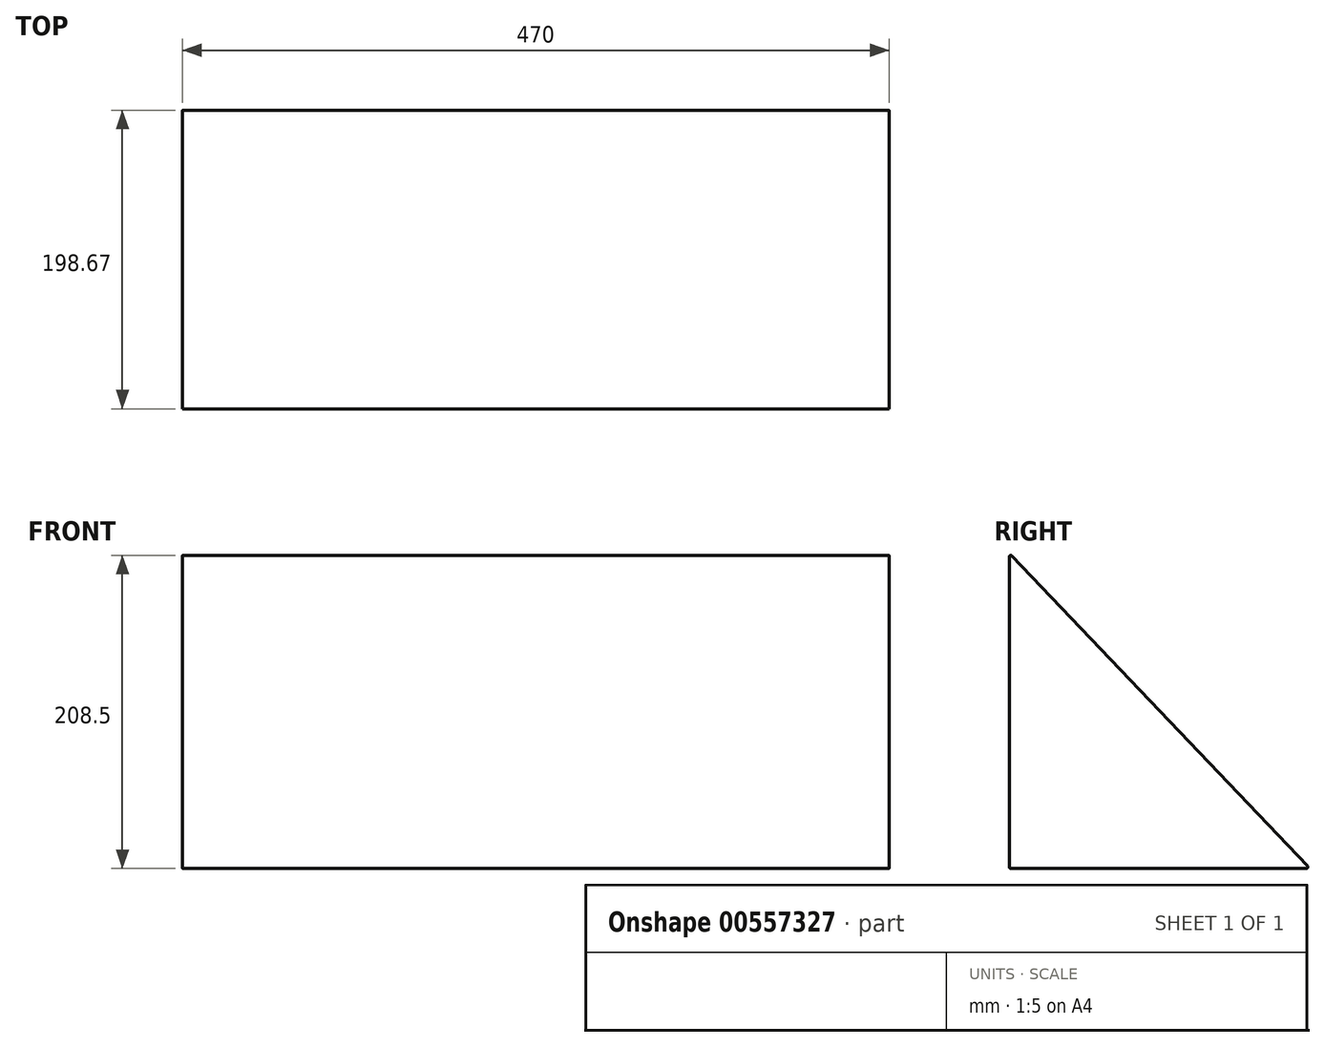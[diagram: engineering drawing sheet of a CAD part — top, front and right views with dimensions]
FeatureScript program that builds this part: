
annotation { "Feature Type Name" : "Feature", "Feature Type Description" : "" }
export const myFeature = defineFeature(function(context is Context, id is Id, definition is map)
    precondition{}
    {
        {
            var Q0;
            Q0=qCreatedBy(makeId("Right.planeOp"),FACE);
            var sketch = newSketch(context, id + "F0", { "sketchPlane" : qUnion([Q0])});
            skLineSegment(sketch, "E0", {"start": v(0, 0) * mm, "end": v(0, 210) * mm});
            skLineSegment(sketch, "E1", {"start": v(0, 210) * mm, "end": v(200, 0) * mm});
            skLineSegment(sketch, "E2", {"start": v(200, 0) * mm, "end": v(0, 0) * mm});
            skSolve(sketch);
        }
        {
            var Q0;
            Q0 = qSketchRegion(id + "F0", true);
            extrude(context, id + "F1", {"entities" : qUnion([Q0]), "depth" : 470 * mm, "offsetDistance" : 25.4 * mm});
        }
        {
            var Q0;
            Q0=makeQuery(id+"F1.opExtrude","SWEPT_EDGE",EDGE,{"disambiguationData":[OSD([sQuery(id+"F0.wireOp",EDGE,"E0"),sQuery(id+"F0.wireOp",EDGE,"E1")])]});
            var Q1;
            Q1=makeQuery(id+"F1.opExtrude","SWEPT_EDGE",EDGE,{"disambiguationData":[OSD([sQuery(id+"F0.wireOp",EDGE,"E1"),sQuery(id+"F0.wireOp",EDGE,"E2")])]});
            var Q2;
            Q2=makeQuery(id+"F1.opExtrude","SWEPT_EDGE",EDGE,{"disambiguationData":[OSD([sQuery(id+"F0.wireOp",EDGE,"E0"),sQuery(id+"F0.wireOp",EDGE,"E2")])]});
            fillet(context, id + "F2", {"entities" : qUnion([Q0, Q1, Q2]), "radius" : 1 * mm, "tangentPropagation" : true, "allowEdgeOverflow" : false});
        }
    });
